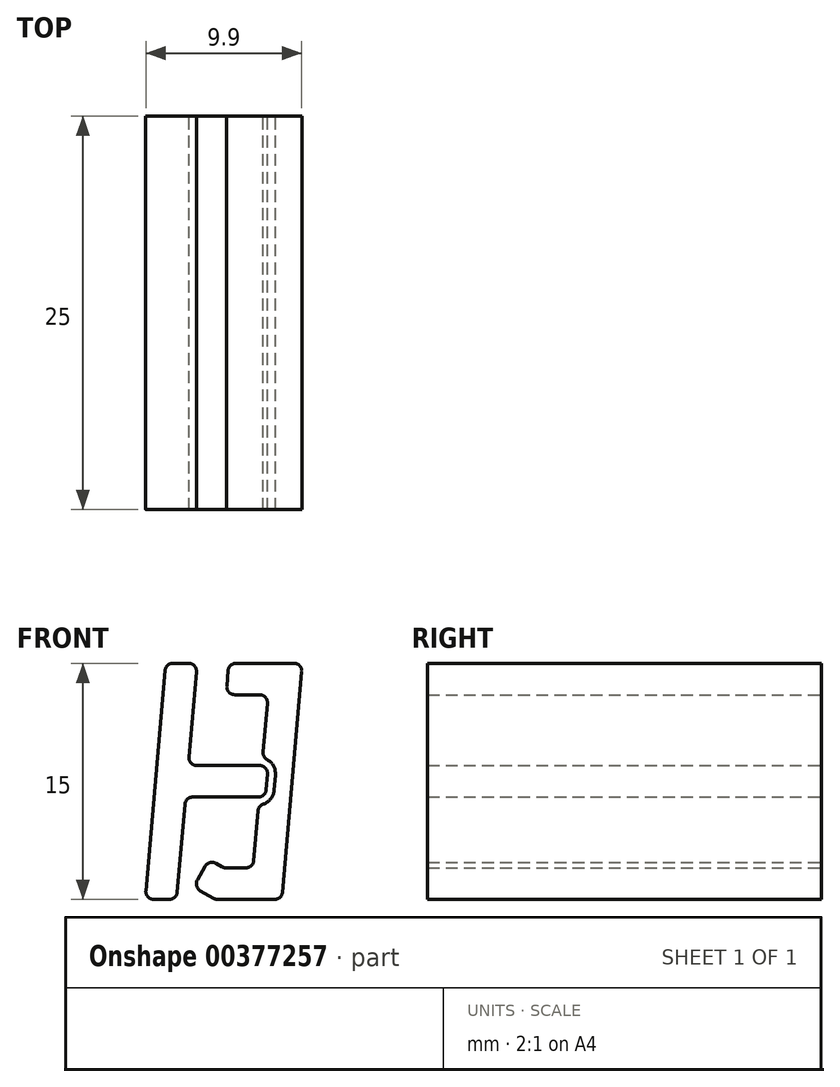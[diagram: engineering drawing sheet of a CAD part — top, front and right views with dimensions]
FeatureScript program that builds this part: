
annotation { "Feature Type Name" : "Feature", "Feature Type Description" : "" }
export const myFeature = defineFeature(function(context is Context, id is Id, definition is map)
    precondition{}
    {
        {
            var Q0;
            Q0=qCreatedBy(makeId("Front.planeOp"),FACE);
            var sketch = newSketch(context, id + "F0", { "sketchPlane" : qUnion([Q0])});
            skLineSegment(sketch, "E0.bottom", {"start": v(5, 7.5) * mm, "end": v(-5, 7.5) * mm, "construction": true});
            skLineSegment(sketch, "E0.top", {"start": v(5, -7.5) * mm, "end": v(-5, -7.5) * mm, "construction": true});
            skLineSegment(sketch, "E0.left", {"start": v(5, 7.5) * mm, "end": v(5, -7.5) * mm, "construction": true});
            skLineSegment(sketch, "E0.right", {"start": v(-5, 7.5) * mm, "end": v(-5, -7.5) * mm, "construction": true});
            skPoint(sketch, "E0.middle", {"position": v(0, 0) * mm});
            skLineSegment(sketch, "E1", {"start": v(-4.95, -6.96) * mm, "end": v(-3.73, 7.04) * mm});
            skLineSegment(sketch, "E2", {"start": v(-3.23, 7.5) * mm, "end": v(-2.23, 7.5) * mm});
            skLineSegment(sketch, "E3", {"start": v(-1.74, 6.96) * mm, "end": v(-2.2, 1.54) * mm});
            skLineSegment(sketch, "E4", {"start": v(-1.71, 1) * mm, "end": v(2.28, 1) * mm});
            skLineSegment(sketch, "E5", {"start": v(2.78, 0.46) * mm, "end": v(2.7, -0.54) * mm});
            skLineSegment(sketch, "E6", {"start": v(2.2, -1) * mm, "end": v(-1.97, -1) * mm});
            skLineSegment(sketch, "E7", {"start": v(-2.47, -1.46) * mm, "end": v(-2.96, -7.04) * mm});
            skLineSegment(sketch, "E8", {"start": v(-3.46, -7.5) * mm, "end": v(-4.45, -7.5) * mm});
            skLineSegment(sketch, "E9", {"start": v(0.78, 7.5) * mm, "end": v(4.45, 7.5) * mm});
            skLineSegment(sketch, "E10", {"start": v(4.95, 6.96) * mm, "end": v(3.73, -7.04) * mm});
            skLineSegment(sketch, "E11", {"start": v(3.23, -7.5) * mm, "end": v(-0.4, -7.5) * mm});
            skLineSegment(sketch, "E12", {"start": v(-0.65, -7.43) * mm, "end": v(-1.5, -6.95) * mm});
            skLineSegment(sketch, "E13", {"start": v(-1.68, -6.26) * mm, "end": v(-1.18, -5.4) * mm});
            skLineSegment(sketch, "E14", {"start": v(-0.5, -5.22) * mm, "end": v(-0.12, -5.43) * mm});
            skLineSegment(sketch, "E15", {"start": v(0.13, -5.5) * mm, "end": v(1.4, -5.5) * mm});
            skLineSegment(sketch, "E16", {"start": v(1.9, -5.04) * mm, "end": v(2.17, -1.88) * mm});
            skLineSegment(sketch, "E17", {"start": v(2.27, 5.5) * mm, "end": v(0.7, 5.5) * mm});
            skLineSegment(sketch, "E18", {"start": v(0.2, 6.04) * mm, "end": v(0.28, 7.04) * mm});
            skLineSegment(sketch, "E19", {"start": v(0, 0) * mm, "end": v(2.74, 0) * mm, "construction": true});
            skPoint(sketch, "E19.endSnap0", {"position": v(2.74, 0) * mm});
            skPoint(sketch, "E20.visualSharp", {"position": v(-3.69, 7.5) * mm});
            skArc(sketch, "E20.filletArc", {"start": v(-3.23, 7.5) * mm, "mid": v(-3.57, 7.37) * mm, "end": v(-3.73, 7.04) * mm});
            skPoint(sketch, "E21.visualSharp", {"position": v(-1.69, 7.5) * mm});
            skArc(sketch, "E22.filletArc", {"start": v(-1.74, 6.96) * mm, "mid": v(-1.86, 7.34) * mm, "end": v(-2.23, 7.5) * mm});
            skPoint(sketch, "E23.visualSharp", {"position": v(-2.26, 1) * mm});
            skArc(sketch, "E23.filletArc", {"start": v(-2.2, 1.54) * mm, "mid": v(-2.08, 1.16) * mm, "end": v(-1.71, 1) * mm});
            skPoint(sketch, "E24.visualSharp", {"position": v(2.83, 1) * mm});
            skArc(sketch, "E24.filletArc", {"start": v(2.78, 0.46) * mm, "mid": v(2.65, 0.84) * mm, "end": v(2.28, 1) * mm});
            skPoint(sketch, "E25.visualSharp", {"position": v(2.65, -1) * mm});
            skArc(sketch, "E25.filletArc", {"start": v(2.2, -1) * mm, "mid": v(2.53, -0.87) * mm, "end": v(2.7, -0.54) * mm});
            skPoint(sketch, "E26.visualSharp", {"position": v(-2.43, -1) * mm});
            skArc(sketch, "E26.filletArc", {"start": v(-1.97, -1) * mm, "mid": v(-2.31, -1.13) * mm, "end": v(-2.47, -1.46) * mm});
            skPoint(sketch, "E27.visualSharp", {"position": v(-3, -7.5) * mm});
            skArc(sketch, "E27.filletArc", {"start": v(-3.46, -7.5) * mm, "mid": v(-3.12, -7.37) * mm, "end": v(-2.96, -7.04) * mm});
            skPoint(sketch, "E28.visualSharp", {"position": v(-5, -7.5) * mm});
            skArc(sketch, "E28.filletArc", {"start": v(-4.95, -6.96) * mm, "mid": v(-4.82, -7.34) * mm, "end": v(-4.45, -7.5) * mm});
            skPoint(sketch, "E29.visualSharp", {"position": v(-1.93, -6.7) * mm});
            skArc(sketch, "E29.filletArc", {"start": v(-1.68, -6.26) * mm, "mid": v(-1.73, -6.64) * mm, "end": v(-1.5, -6.95) * mm});
            skPoint(sketch, "E30.visualSharp", {"position": v(-0.93, -4.97) * mm});
            skArc(sketch, "E30.filletArc", {"start": v(-0.5, -5.22) * mm, "mid": v(-0.87, -5.17) * mm, "end": v(-1.18, -5.4) * mm});
            skPoint(sketch, "E31.visualSharp", {"position": v(0, -5.5) * mm});
            skArc(sketch, "E31.filletArc", {"start": v(-0.12, -5.43) * mm, "mid": v(0, -5.48) * mm, "end": v(0.13, -5.5) * mm});
            skPoint(sketch, "E32.visualSharp", {"position": v(1.86, -5.5) * mm});
            skArc(sketch, "E32.filletArc", {"start": v(1.4, -5.5) * mm, "mid": v(1.73, -5.37) * mm, "end": v(1.9, -5.04) * mm});
            skPoint(sketch, "E33.visualSharp", {"position": v(2.82, 5.5) * mm});
            skArc(sketch, "E33.filletArc", {"start": v(2.77, 4.96) * mm, "mid": v(2.64, 5.34) * mm, "end": v(2.27, 5.5) * mm});
            skPoint(sketch, "E34.visualSharp", {"position": v(0.14, 5.5) * mm});
            skArc(sketch, "E34.filletArc", {"start": v(0.2, 6.04) * mm, "mid": v(0.32, 5.66) * mm, "end": v(0.7, 5.5) * mm});
            skPoint(sketch, "E35.visualSharp", {"position": v(0.32, 7.5) * mm});
            skArc(sketch, "E35.filletArc", {"start": v(0.78, 7.5) * mm, "mid": v(0.44, 7.37) * mm, "end": v(0.28, 7.04) * mm});
            skPoint(sketch, "E36.visualSharp", {"position": v(5, 7.5) * mm});
            skArc(sketch, "E36.filletArc", {"start": v(4.95, 6.96) * mm, "mid": v(4.82, 7.34) * mm, "end": v(4.45, 7.5) * mm});
            skPoint(sketch, "E37.visualSharp", {"position": v(3.69, -7.5) * mm});
            skArc(sketch, "E37.filletArc", {"start": v(3.23, -7.5) * mm, "mid": v(3.57, -7.37) * mm, "end": v(3.73, -7.04) * mm});
            skPoint(sketch, "E38.visualSharp", {"position": v(-0.54, -7.5) * mm});
            skArc(sketch, "E38.filletArc", {"start": v(-0.65, -7.43) * mm, "mid": v(-0.53, -7.48) * mm, "end": v(-0.4, -7.5) * mm});
            skArc(sketch, "E39.1", {"start": v(2.51, -1.45) * mm, "mid": v(2.98, -1.12) * mm, "end": v(3.19, -0.59) * mm});
            skLineSegment(sketch, "E40.0", {"start": v(3.28, 0.41) * mm, "end": v(3.19, -0.59) * mm});
            skArc(sketch, "E41.1", {"start": v(3.28, 0.41) * mm, "mid": v(3.16, 0.97) * mm, "end": v(2.76, 1.38) * mm});
            skLineSegment(sketch, "E42.trimOffspring", {"start": v(2.5, 1.86) * mm, "end": v(2.77, 4.96) * mm});
            skLineSegment(sketch, "E43.trimOffspring", {"start": v(2.25, -1) * mm, "end": v(2.42, 1) * mm});
            skPoint(sketch, "E44.visualSharp", {"position": v(2.2, -1.5) * mm});
            skArc(sketch, "E44.filletArc", {"start": v(2.51, -1.45) * mm, "mid": v(2.28, -1.61) * mm, "end": v(2.17, -1.88) * mm});
            skPoint(sketch, "E45.visualSharp", {"position": v(2.47, 1.48) * mm});
            skArc(sketch, "E45.filletArc", {"start": v(2.5, 1.86) * mm, "mid": v(2.56, 1.58) * mm, "end": v(2.76, 1.38) * mm});
            skSolve(sketch);
        }
        {
            var Q0;
            Q0 = qSketchRegion(id + "F0", true);
            extrude(context, id + "F1", {"entities" : qUnion([Q0]), "depth" : 25 * mm});
        }
    });
